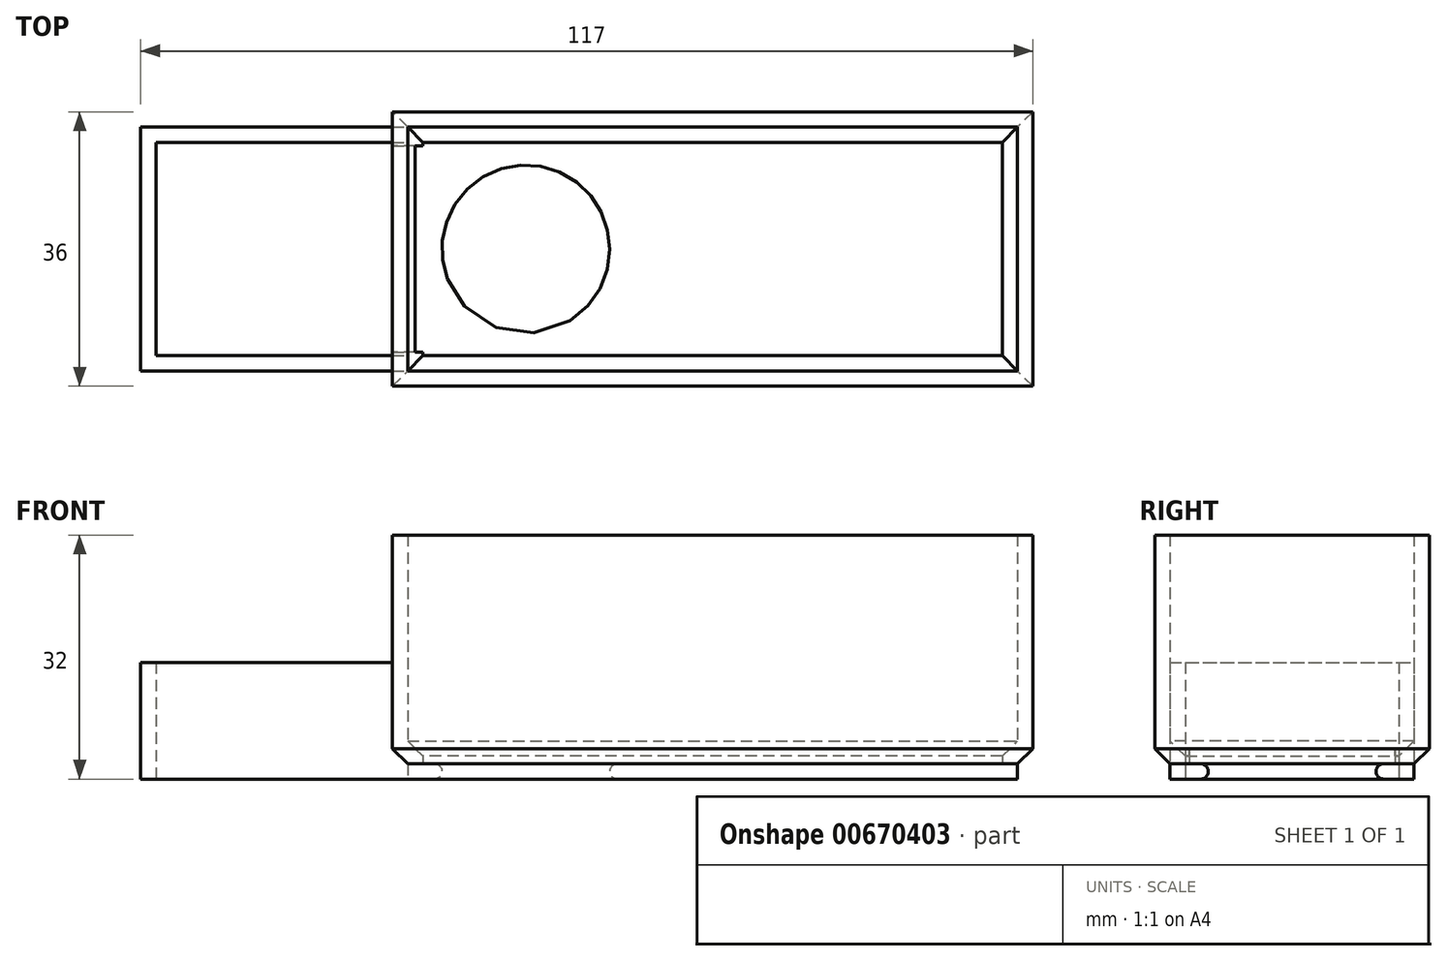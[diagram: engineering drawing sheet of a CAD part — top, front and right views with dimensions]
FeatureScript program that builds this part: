
annotation { "Feature Type Name" : "Feature", "Feature Type Description" : "" }
export const myFeature = defineFeature(function(context is Context, id is Id, definition is map)
    precondition{}
    {
        {
            var Q0;
            Q0=qCreatedBy(makeId("Top.planeOp"),FACE);
            var sketch = newSketch(context, id + "F0", { "sketchPlane" : qUnion([Q0])});
            skLineSegment(sketch, "E0.bottom", {"start": v(-40, 16) * mm, "end": v(40, 16) * mm});
            skLineSegment(sketch, "E0.top", {"start": v(-40, -16) * mm, "end": v(40, -16) * mm});
            skLineSegment(sketch, "E0.left", {"start": v(-40, 16) * mm, "end": v(-40, -16) * mm});
            skLineSegment(sketch, "E0.right", {"start": v(40, 16) * mm, "end": v(40, -16) * mm});
            skPoint(sketch, "E0.middle", {"position": v(0, 0) * mm});
            skLineSegment(sketch, "E1.0", {"start": v(-42, 18) * mm, "end": v(42, 18) * mm});
            skLineSegment(sketch, "E1.1", {"start": v(-42, 18) * mm, "end": v(-42, -18) * mm});
            skLineSegment(sketch, "E1.2", {"start": v(-42, -18) * mm, "end": v(42, -18) * mm});
            skLineSegment(sketch, "E1.3", {"start": v(42, 18) * mm, "end": v(42, -18) * mm});
            skLineSegment(sketch, "E2.0", {"start": v(-38, 14) * mm, "end": v(38, 14) * mm});
            skLineSegment(sketch, "E2.1", {"start": v(-38, 14) * mm, "end": v(-38, -14) * mm});
            skLineSegment(sketch, "E2.2", {"start": v(-38, -14) * mm, "end": v(38, -14) * mm});
            skLineSegment(sketch, "E2.3", {"start": v(38, 14) * mm, "end": v(38, -14) * mm});
            skCircle(sketch, "E3", {"center": v(-24.5, 0) * mm, "radius": 11 * mm});
            skSolve(sketch);
        }
        {
            var Q0;
            Q0=makeQuery(id+"F0.imprint","IMPRINT",FACE,{"disambiguationData":[TD([[makeQuery(id+"F0.imprint","IMPRINT",EDGE,{"derivedFrom":sQuery(id+"F0.wireOp",EDGE,"E0.bottom")}),1.0]])]});
            extrude(context, id + "F1", {"entities" : qUnion([Q0]), "depth" : 30 * mm, "offsetDistance" : 25 * mm});
        }
        {
            var Q0;
            Q0=makeQuery(id+"F0.imprint","IMPRINT",FACE,{"disambiguationData":[TD([[makeQuery(id+"F0.imprint","IMPRINT",EDGE,{"derivedFrom":sQuery(id+"F0.wireOp",EDGE,"E0.bottom")}),-1.0]])]});
            extrude(context, id + "F2", {"entities" : qUnion([Q0]), "operationType" : NewBodyOperationType.ADD, "depth" : 3 * mm, "offsetDistance" : 25 * mm});
        }
        {
            var Q0;
            Q0=makeQuery(id+"F0.imprint","IMPRINT",FACE,{"disambiguationData":[TD([[makeQuery(id+"F0.imprint","IMPRINT",EDGE,{"derivedFrom":sQuery(id+"F0.wireOp",EDGE,"E0.bottom")}),-1.0]])]});
            var Q1;
            Q1=makeQuery(id+"F0.imprint","IMPRINT",FACE,{"disambiguationData":[TD([[makeQuery(id+"F0.imprint","IMPRINT",EDGE,{"derivedFrom":sQuery(id+"F0.wireOp",EDGE,"E2.0")}),-1.0]])]});
            extrude(context, id + "F3", {"entities" : qUnion([Q0, Q1]), "operationType" : NewBodyOperationType.ADD, "oppositeDirection" : true, "depth" : 2 * mm, "offsetDistance" : 25 * mm});
        }
        {
            var Q0;
            Q0=makeQuery(id+"F1.opExtrude","CAP_EDGE",EDGE,{"disambiguationData":[OSD([sQuery(id+"F0.wireOp",EDGE,"E1.0")])],"isStart":true});
            var Q1;
            Q1=makeQuery(id+"F1.opExtrude","CAP_EDGE",EDGE,{"disambiguationData":[OSD([sQuery(id+"F0.wireOp",EDGE,"E1.2")])],"isStart":true});
            var Q2;
            Q2=makeQuery(id+"F1.opExtrude","CAP_EDGE",EDGE,{"disambiguationData":[OSD([sQuery(id+"F0.wireOp",EDGE,"E1.3")])],"isStart":true});
            var Q3;
            Q3=makeQuery(id+"F1.opExtrude","CAP_EDGE",EDGE,{"disambiguationData":[OSD([sQuery(id+"F0.wireOp",EDGE,"E1.1")])],"isStart":true});
            chamfer(context, id + "F4", {"entities" : qUnion([Q0, Q1, Q2, Q3]), "width" : 2 * mm, "tangentPropagation" : true});
        }
        {
            var Q0;
            Q0=makeQuery(id+"F2.opExtrude","CAP_EDGE",EDGE,{"disambiguationData":[OSD([sQuery(id+"F0.wireOp",EDGE,"E2.2")])],"isStart":false});
            var Q1;
            Q1=makeQuery(id+"F2.opExtrude","CAP_EDGE",EDGE,{"disambiguationData":[OSD([sQuery(id+"F0.wireOp",EDGE,"E2.3")])],"isStart":false});
            var Q2;
            Q2=makeQuery(id+"F2.opExtrude","CAP_EDGE",EDGE,{"disambiguationData":[OSD([sQuery(id+"F0.wireOp",EDGE,"E2.0")])],"isStart":false});
            var Q3;
            Q3=makeQuery(id+"F2.opExtrude","CAP_EDGE",EDGE,{"disambiguationData":[OSD([sQuery(id+"F0.wireOp",EDGE,"E2.1")])],"isStart":false});
            chamfer(context, id + "F5", {"entities" : qUnion([Q0, Q1, Q2, Q3]), "width" : 2 * mm, "tangentPropagation" : true});
        }
        {
            var Q0;
            Q0=makeQuery(id+"F1.opExtrude","SWEPT_FACE",FACE,{"disambiguationData":[OSD([sQuery(id+"F0.wireOp",EDGE,"E1.1")])]});
            var sketch = newSketch(context, id + "F6", { "sketchPlane" : qUnion([Q0])});
            skLineSegment(sketch, "E4.bottom", {"start": v(-13.5, 0) * mm, "end": v(13.5, 0) * mm});
            skLineSegment(sketch, "E4.top", {"start": v(-13.5, 2.3) * mm, "end": v(13.5, 2.3) * mm});
            skLineSegment(sketch, "E4.left", {"start": v(-13.5, 0) * mm, "end": v(-13.5, 2.3) * mm});
            skLineSegment(sketch, "E4.right", {"start": v(13.5, 0) * mm, "end": v(13.5, 2.3) * mm});
            skSolve(sketch);
        }
        {
            var Q0;
            {var subQ0=sQuery(id+"F6.wireOp",EDGE,"E4.bottom");Q0=makeQuery(id+"F6.imprint","IMPRINT",FACE,{"disambiguationData":[TD([[makeQuery(id+"F6.imprint","IMPRINT",EDGE,{"derivedFrom":subQ0}),1.0]])]});}
            extrude(context, id + "F7", {"entities" : qUnion([Q0]), "operationType" : NewBodyOperationType.REMOVE, "oppositeDirection" : true, "depth" : 5 * mm, "offsetDistance" : 25 * mm});
        }
        {
            var Q0;
            Q0=makeQuery(id+"F3.opExtrude","CAP_FACE",FACE,{"disambiguationData":[OSD([sQuery(id+"F0.wireOp",EDGE,"E0.bottom"),sQuery(id+"F0.wireOp",EDGE,"E0.top"),sQuery(id+"F0.wireOp",EDGE,"E0.left"),sQuery(id+"F0.wireOp",EDGE,"E0.right")])],"isStart":false});
            var sketch = newSketch(context, id + "F8", { "sketchPlane" : qUnion([Q0])});
            skLineSegment(sketch, "E5.bottom", {"start": v(-40, 16) * mm, "end": v(-75, 16) * mm});
            skLineSegment(sketch, "E5.top", {"start": v(-40, -16) * mm, "end": v(-75, -16) * mm});
            skLineSegment(sketch, "E5.left", {"start": v(-40, 16) * mm, "end": v(-40, -16) * mm});
            skLineSegment(sketch, "E5.right", {"start": v(-75, 16) * mm, "end": v(-75, -16) * mm});
            skLineSegment(sketch, "E6.0", {"start": v(-40, -14) * mm, "end": v(-73, -14) * mm});
            skLineSegment(sketch, "E6.1", {"start": v(-73, 14) * mm, "end": v(-73, -14) * mm});
            skLineSegment(sketch, "E6.2", {"start": v(-40, 14) * mm, "end": v(-73, 14) * mm});
            skSolve(sketch);
        }
        {
            var Q0;
            {var subQ1=sQuery(id+"F8.wireOp",EDGE,"E5.bottom");Q0=makeQuery(id+"F8.imprint","IMPRINT",FACE,{"disambiguationData":[TD([[makeQuery(id+"F8.imprint","IMPRINT",EDGE,{"derivedFrom":subQ1}),1.0]])]});}
            extrude(context, id + "F9", {"entities" : qUnion([Q0]), "operationType" : NewBodyOperationType.ADD, "oppositeDirection" : true, "depth" : 15.3 * mm, "offsetDistance" : 25 * mm});
        }
        {
            var Q0;
            Q0=makeQuery(id+"F3.opExtrude","CAP_EDGE",EDGE,{"disambiguationData":[OSD([sQuery(id+"F0.wireOp",EDGE,"E3")])],"isStart":false});
            var Q1;
            Q1=makeQuery(id+"F3.opExtrude","CAP_EDGE",EDGE,{"disambiguationData":[OSD([sQuery(id+"F0.wireOp",EDGE,"E3")])],"isStart":true});
            fillet(context, id + "F10", {"entities" : qUnion([Q0, Q1]), "radius" : 1 * mm, "tangentPropagation" : true, "allowEdgeOverflow" : false});
        }
    });
